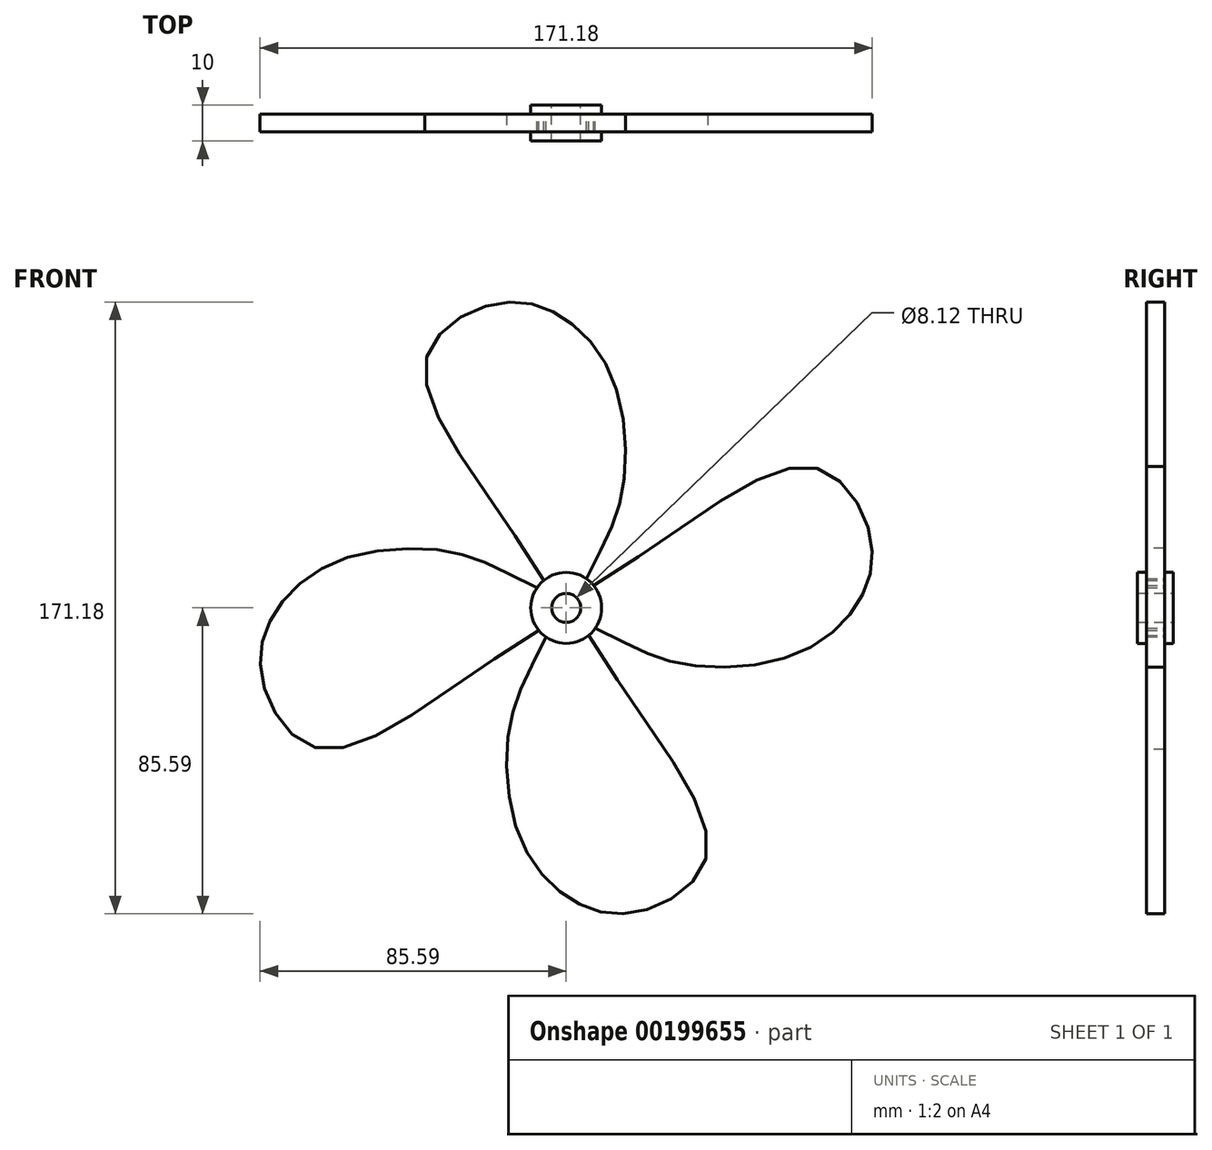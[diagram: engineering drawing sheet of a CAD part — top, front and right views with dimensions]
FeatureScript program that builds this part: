
annotation { "Feature Type Name" : "Feature", "Feature Type Description" : "" }
export const myFeature = defineFeature(function(context is Context, id is Id, definition is map)
    precondition{}
    {
        {
            var Q0;
            Q0=qCreatedBy(makeId("Front.planeOp"),FACE);
            var sketch = newSketch(context, id + "F0", { "sketchPlane" : qUnion([Q0])});
            skCircle(sketch, "E0", {"center": v(0, 0) * mm, "radius": 4.06 * mm});
            skCircle(sketch, "E1", {"center": v(0, 0) * mm, "radius": 9.91 * mm});
            skFitSpline(sketch, "E2", {"points": [v(-6.31, 7.65) * mm, v(-39.39, 68.39) * mm, v(-21.36, 84.72) * mm, v(-2.9, 82.4) * mm, v(12.7, 64.93) * mm, v(15.84, 33.15) * mm, v(5.67, 8.13) * mm], "startDerivative": vector(-174.64, 293.4) * mm, "endDerivative": vector(-100.88, -207.29) * mm});
            skSolve(sketch);
        }
        {
            var Q0;
            {var subQ0=sQuery(id+"F0.wireOp",EDGE,"E2");Q0=makeQuery(id+"F0.imprint","IMPRINT",FACE,{"disambiguationData":[TD([[makeQuery(id+"F0.imprint","IMPRINT",EDGE,{"derivedFrom":subQ0}),-1.0]])]});}
            extrude(context, id + "F1", {"entities" : qUnion([Q0]), "endBound" : BoundingType.SYMMETRIC, "depth" : 5 * mm});
        }
        {
            var Q0;
            Q0=qCreatedBy(makeId("Right.planeOp"),FACE);
            var sketch = newSketch(context, id + "F2", { "sketchPlane" : qUnion([Q0])});
            skLineSegment(sketch, "E3", {"start": v(-25.87, 0) * mm, "end": v(31.62, 0) * mm});
            skSolve(sketch);
        }
        {
            var Q0;
            Q0=makeQuery(id+"F1.opExtrude","SWEPT_BODY",BODY,{"disambiguationData":[OSD([sQuery(id+"F0.wireOp",EDGE,"E1"),sQuery(id+"F0.wireOp",EDGE,"E2")])]});
            var Q1;
            Q1=sQuery(id+"F2.wireOp",EDGE,"E3");
            circularPattern(context, id + "F3", {"entities" : qUnion([Q0]), "axis" : qUnion([Q1]), "angle" : 360 * degree, "instanceCount" : 4, "equalSpace" : true});
        }
        {
            var Q0;
            Q0=makeQuery(id+"F0.imprint","IMPRINT",FACE,{"disambiguationData":[TD([[makeQuery(id+"F0.imprint","IMPRINT",EDGE,{"derivedFrom":sQuery(id+"F0.wireOp",EDGE,"E0")}),-1.0]])]});
            extrude(context, id + "F4", {"entities" : qUnion([Q0]), "operationType" : NewBodyOperationType.ADD, "endBound" : BoundingType.SYMMETRIC, "depth" : 10 * mm});
        }
    });
